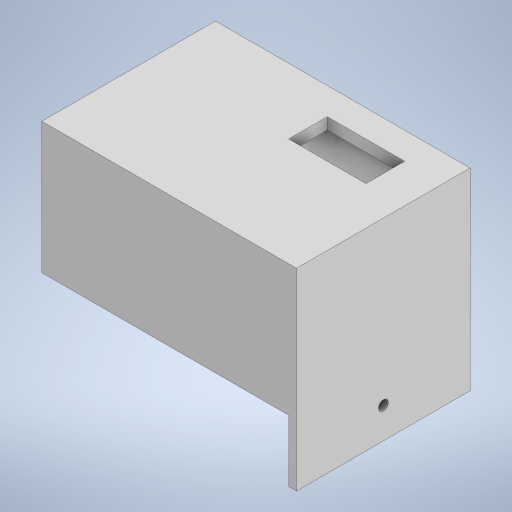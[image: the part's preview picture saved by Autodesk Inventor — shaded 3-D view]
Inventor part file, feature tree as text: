
AUTODESK INVENTOR PART (.ipt)
format: ipt  version: 2024 (Build 280153000, 153)  size: 275,456 bytes
history: native  units: in
note: dims shown in document units (in); Inventor stores cm internally (conversion verified against a paired STEP export)
features: extrude x7, sketch x7
ambient origin geometry x8: Origin, YZ Plane, XZ Plane, XY Plane, X Axis, Y Axis, Z Axis, Center Point
bodies: Body1 (feature_tree)
feature tree (14):
  extrude  "Extrusion51"  Depth=1.7717in
  extrude  "Extrusion52"  Depth=0.1181in
  extrude  "Extrusion53"  Depth=0.1181in
  extrude  "Extrusion54"  Depth=0.315in
  extrude  "Extrusion55"  Depth=0.7874in
  extrude  "Extrusion56"  Depth=1.2205in TaperAngle=0.0deg
  extrude  "Extrusion57"  Depth=1.7717in
  sketch  "Sketch94"  dims[d270=2.5197in d271=1.7717in]
  sketch  "Sketch96"  dims[d272=0.1181in d273=0.0in d274=0.1181in]
  sketch  "Sketch97"  dims[d275=1.2205in d276=0.0in d277=0.1181in]
  sketch  "Sketch98"  dims[d278=1.2205in d279=0.0in d280=0.315in]
  sketch  "Sketch99"  dims[d281=0.2756in d282=0.7874in]
  sketch  "Sketch100"  dims[d283=0.3937in d284=1.2205in d285=0.0in]
  sketch  "Sketch101"  dims[d286=0.0787in d287=1.7717in d288=1.9685in d289=0.0in d290=0.1181in d291=0.5118in d292=0.0in d293=0.8858in d294=0.315in d295=0.0984in d296=0.5118in d297=0.0in d42=0.0197in d43=0.0344in d44=0.0197in d45=0.0344in d46=0.0in d47=0.0in d48=0.0in d49=0.0in d50=0.0in d51=0.0in d52=0.0in d53=0.0in d55=0.0197in d56=0.0344in d57=0.0197in d58=0.0344in d60=0.0197in d61=0.0344in d62=0.0197in d63=0.0344in d72=0.0197in d73=0.0344in d74=0.0197in d75=0.0344in d179=0.0197in d180=0.0344in d181=0.0197in d182=0.0344in d211=0.0197in d212=0.0344in d213=0.0197in d214=0.0344in d235=0.0197in d236=0.0344in d237=0.0197in d238=0.0344in d243=0.0197in d244=0.0344in d245=0.0197in d246=0.0344in]
